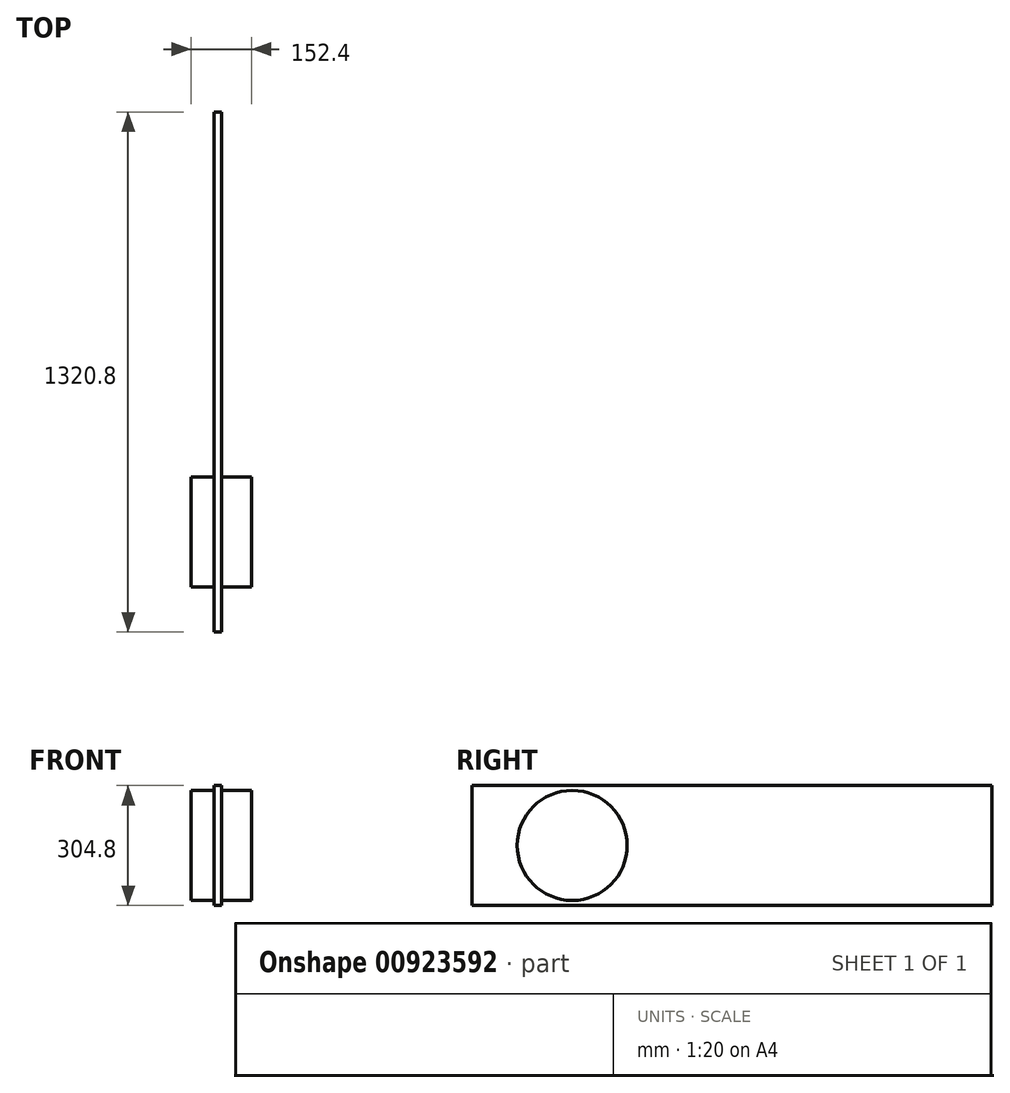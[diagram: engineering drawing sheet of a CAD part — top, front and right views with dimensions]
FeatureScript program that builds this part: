
annotation { "Feature Type Name" : "Feature", "Feature Type Description" : "" }
export const myFeature = defineFeature(function(context is Context, id is Id, definition is map)
    precondition{}
    {
        {
            var Q0;
            Q0=qCreatedBy(makeId("Right.planeOp"),FACE);
            var sketch = newSketch(context, id + "F0", { "sketchPlane" : qUnion([Q0])});
            skLineSegment(sketch, "E0.bottom", {"start": v(0, 0) * mm, "end": v(1320.8, 0) * mm});
            skLineSegment(sketch, "E0.top", {"start": v(0, 304.8) * mm, "end": v(1320.8, 304.8) * mm});
            skLineSegment(sketch, "E0.left", {"start": v(0, 0) * mm, "end": v(0, 304.8) * mm});
            skLineSegment(sketch, "E0.right", {"start": v(1320.8, 0) * mm, "end": v(1320.8, 304.8) * mm});
            skSolve(sketch);
        }
        {
            var Q0;
            Q0 = qSketchRegion(id + "F0", true);
            extrude(context, id + "F1", {"entities" : qUnion([Q0]), "depth" : 19.05 * mm, "offsetDistance" : 25.4 * mm});
        }
        {
            var Q0;
            Q0=makeQuery(id+"F1.opExtrude","CAP_FACE",FACE,{"disambiguationData":[OSD([sQuery(id+"F0.wireOp",EDGE,"E0.bottom"),sQuery(id+"F0.wireOp",EDGE,"E0.top"),sQuery(id+"F0.wireOp",EDGE,"E0.left"),sQuery(id+"F0.wireOp",EDGE,"E0.right")])],"isStart":false});
            var sketch = newSketch(context, id + "F2", { "sketchPlane" : qUnion([Q0])});
            skCircle(sketch, "E1", {"center": v(254, 152.4) * mm, "radius": 139.7 * mm});
            skSolve(sketch);
        }
        {
            var Q0;
            Q0 = qSketchRegion(id + "F2", true);
            extrude(context, id + "F3", {"entities" : qUnion([Q0]), "operationType" : NewBodyOperationType.ADD, "depth" : 76.2 * mm, "offsetDistance" : 25.4 * mm, "hasSecondDirection" : true, "secondDirectionOppositeDirection" : true, "secondDirectionDepth" : 76.2 * mm});
        }
    });
